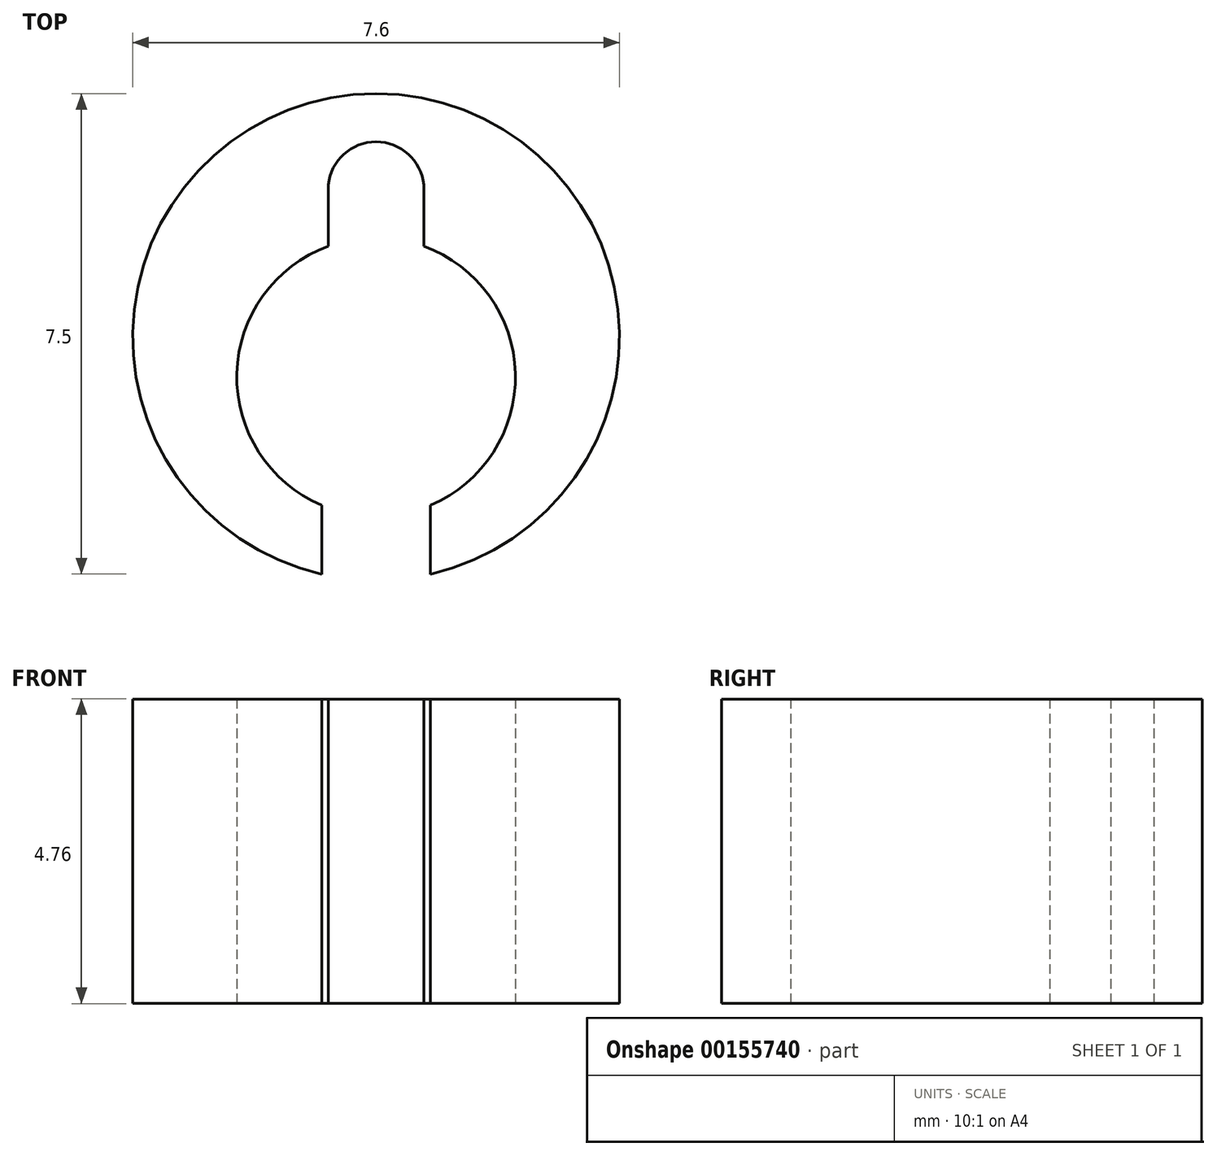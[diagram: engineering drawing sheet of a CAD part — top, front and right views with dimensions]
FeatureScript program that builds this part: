
annotation { "Feature Type Name" : "Feature", "Feature Type Description" : "" }
export const myFeature = defineFeature(function(context is Context, id is Id, definition is map)
    precondition{}
    {
        {
            var Q0;
            Q0=qCreatedBy(makeId("Top.planeOp"),FACE);
            var sketch = newSketch(context, id + "F0", { "sketchPlane" : qUnion([Q0])});
            skArc(sketch, "E0", {"start": v(0.85, -3.7) * mm, "mid": v(0, 3.8) * mm, "end": v(-0.85, -3.7) * mm});
            skArc(sketch, "E1", {"start": v(0.85, -2.63) * mm, "mid": v(2.17, -0.57) * mm, "end": v(0.75, 1.42) * mm});
            skLineSegment(sketch, "E2", {"start": v(-0.85, -2.63) * mm, "end": v(-0.85, -3.7) * mm});
            skLineSegment(sketch, "E3.MirrorCS", {"start": v(0.85, -2.63) * mm, "end": v(0.85, -3.7) * mm});
            skLineSegment(sketch, "E4", {"start": v(-0.75, 2.37) * mm, "end": v(-0.75, 1.42) * mm});
            skLineSegment(sketch, "E5.MirrorCS", {"start": v(0.75, 2.37) * mm, "end": v(0.75, 1.42) * mm});
            skArc(sketch, "E6.trimOffspring", {"start": v(0.75, 2.37) * mm, "mid": v(0, 3.05) * mm, "end": v(-0.75, 2.37) * mm});
            skArc(sketch, "E7.trimOffspring", {"start": v(-0.75, 1.42) * mm, "mid": v(-2.17, -0.57) * mm, "end": v(-0.85, -2.63) * mm});
            skPoint(sketch, "E8.center.orphan", {"position": v(0, 2.27) * mm});
            skSolve(sketch);
        }
        {
            var Q0;
            Q0 = qSketchRegion(id + "F0", true);
            extrude(context, id + "F1", {"entities" : qUnion([Q0]), "endBound" : BoundingType.SYMMETRIC, "depth" : 4.75 * mm});
        }
    });
